# Revit family: Casement_28_E_Side_Hung_Standard
name_source: partatom
category: Windows
revit_build: Autodesk Revit 2014 (Build: 20130308_1515(x64)
units: mm (PartAtom-declared; Revit-internal decimal feet)

## types (17) — shared parameters
Aluminium Thickness = 1 mm  [stored 0.00328084 ft]
Area Pane Left Top = 0.52 m²
Bead SG Gap = 13 mm  [stored 0.0426509 ft]
Casement Dimension = 28 mm  [stored 0.0918635 ft]
Custom Sash Height = 1154 mm  [stored 3.78609 ft]
Custom Sash Width = 554 mm  [stored 1.81759 ft]
Default Sill Height = 800 mm  [stored 2.62467 ft]
Depth Bead = 14 mm  [stored 0.0459318 ft]
Description = Window 28mm, Type E side hung
Frame Center Offset = 14 mm  [stored 0.0459318 ft]
Height Panel 1 = 1139 mm  [stored 3.73688 ft]
Height Sash = 1124 mm  [stored 3.68766 ft]
Height Sash Opening = 1154 mm  [stored 3.78609 ft]
Length Transom = 540 mm  [stored 1.77165 ft]
Limit Fixed Pane Height Max = 1800 mm  [stored 5.90551 ft]
Limit Fixed Pane Height Min = 200 mm  [stored 0.656168 ft]
Limit Fixed Pane Width Max = 1500 mm  [stored 4.92126 ft]
Limit Fixed Pane Width Min = 200 mm  [stored 0.656168 ft]
Limit Sash Height Max = 1200 mm
Limit Sash Height Min = 300 mm  [stored 0.984252 ft]
Limit Sash Width Max = 600 mm  [stored 1.9685 ft]
Limit Sash Width Min = 300 mm  [stored 0.984252 ft]
Limit Window Height Max = 1860 mm
Limit Window Height Min = 1430 mm  [stored 4.6916 ft]
Limit Window Width Max = 2130 mm
Limit Window Width Min = 830 mm
Manufacturer = Crealco
Model = Casement 28
Offset Bead SG Center Reversed = 14 mm  [stored 0.0459318 ft]
Offset Mullion Left = 570 mm  [stored 1.87008 ft]
Offset Panel 3 Bead Top = 1200 mm
Offset Panel 4 Left = 600 mm  [stored 1.9685 ft]
Offset Sash Left = 23 mm  [stored 0.0754593 ft]
Offset Sash Top = 23 mm  [stored 0.0754593 ft]
Offset Transom Top = 1170 mm
Offset Window Exterior = 14 mm  [stored 0.0459318 ft]
SG Gasket Thickness = 6 mm  [stored 0.019685 ft]
Sash Center Offset = 11 mm  [stored 0.0360892 ft]
Sash Overlap = 7 mm  [stored 0.0229659 ft]
Sash Spacing Inner = 8 mm  [stored 0.0262467 ft]
Single Glazing = Yes
URL = http://www.crealco.co.za
Wall Closure = By host
Width Bead = 15 mm  [stored 0.0492126 ft]
Width Fixed Pane Bottom LHS = 540 mm  [stored 1.77165 ft]
Width Panel 1 = 540 mm  [stored 1.77165 ft]
Width Profile = 30 mm  [stored 0.0984252 ft]
Width Sash = 524 mm  [stored 1.71916 ft]
Width Sash Opening = 554 mm  [stored 1.81759 ft]
zero-valued in all types: Window Exterior Offset

## per-type parameters (varying)
| type | Area Pane Left Bottom | Area Pane Right | Clearvue SHGC Value | Clearvue U Value | Custom Windload | Custom Window Height | Custom Window Width | Depth Mullion | Energy Advantage SHGC Value | Energy Advantage U Value | Height | Height Fixed Pane Bottom LHS | Height Fixed Pane RHS | Intruderprufe LowE SHGC Value | Intruderprufe LowE U Value | Intruderprufe SHGC Value | Intruderprufe U Value | Length Mullion | Max Pane Area | Mullion Depth Windload Based | Width | Width Fixed Pane RHS | Windload Design |
| 28-0915S-1000Pa | 0.13 m² | 0.36 m² | 0.6 | 6.27 | 1000 mm  [stored 3.28084 ft] | 1490 mm  [stored 4.88845 ft] | 890 mm  [stored 2.91995 ft] | 54 mm  [stored 0.177165 ft] | 0.541 | 4.86 | 1490 mm  [stored 4.88845 ft] | 260 mm  [stored 0.853018 ft] | 1430 mm  [stored 4.6916 ft] | 0.504 | 4.77 | 0.571 | 6.2 | 1490 mm  [stored 4.88845 ft] | 0.52 m² | 54 mm  [stored 0.177165 ft] | 890 mm  [stored 2.91995 ft] | 260 mm  [stored 0.853018 ft] | 1000 mm  [stored 3.28084 ft] |
| 28-1215S-1000Pa | 0.13 m² | 0.78 m² | 0.65 | 6.18 | 1000 mm  [stored 3.28084 ft] | 1490 mm  [stored 4.88845 ft] | 1190 mm  [stored 3.9042 ft] | 54 mm  [stored 0.177165 ft] | 0.582 | 4.63 | 1490 mm  [stored 4.88845 ft] | 260 mm  [stored 0.853018 ft] | 1430 mm  [stored 4.6916 ft] | 0.545 | 4.53 | 0.617 | 6.1 | 1490 mm  [stored 4.88845 ft] | 0.78 m² | 54 mm  [stored 0.177165 ft] | 1190 mm  [stored 3.9042 ft] | 560 mm | 1000 mm  [stored 3.28084 ft] |
| 28-1215S-2000Pa | 0.13 m² | 0.78 m² | 0.723 | 6.93 | 2000 mm | 1490 mm  [stored 4.88845 ft] | 1190 mm  [stored 3.9042 ft] | 70 mm  [stored 0.229659 ft] | 0.647 | 5.23 | 1490 mm  [stored 4.88845 ft] | 260 mm  [stored 0.853018 ft] | 1430 mm  [stored 4.6916 ft] | 0.606 | 5.11 | 0.672 | 6.79 | 1490 mm  [stored 4.88845 ft] | 0.78 m² | 70 mm  [stored 0.229659 ft] | 1190 mm  [stored 3.9042 ft] | 560 mm | 2000 mm |
| 28-1515S-1000Pa | 0.13 m² | 1.21 m² | 0.68 | 6.13 | 1000 mm  [stored 3.28084 ft] | 1490 mm  [stored 4.88845 ft] | 1490 mm  [stored 4.88845 ft] | 54 mm  [stored 0.177165 ft] | 0.606 | 4.49 | 1490 mm  [stored 4.88845 ft] | 260 mm  [stored 0.853018 ft] | 1430 mm  [stored 4.6916 ft] | 0.569 | 4.38 | 0.644 | 6.04 | 1490 mm  [stored 4.88845 ft] | 1.21 m² | 54 mm  [stored 0.177165 ft] | 1490 mm  [stored 4.88845 ft] | 860 mm | 1000 mm  [stored 3.28084 ft] |
| 28-1515S-1500Pa | 0.13 m² | 1.21 m² | 0.774 | 7.03 | 1500 mm  [stored 4.92126 ft] | 1490 mm  [stored 4.88845 ft] | 1490 mm  [stored 4.88845 ft] | 70 mm  [stored 0.229659 ft] | 0.69 | 5.18 | 1490 mm  [stored 4.88845 ft] | 260 mm  [stored 0.853018 ft] | 1430 mm  [stored 4.6916 ft] | 0.647 | 5.05 | 0.721 | 6.88 | 1490 mm  [stored 4.88845 ft] | 1.21 m² | 70 mm  [stored 0.229659 ft] | 1490 mm  [stored 4.88845 ft] | 860 mm | 1500 mm  [stored 4.92126 ft] |
| 28-0918S-1000Pa | 0.29 m² | 0.43 m² | 0.616 | 6.25 | 1000 mm  [stored 3.28084 ft] | 1790 mm  [stored 5.8727 ft] | 890 mm  [stored 2.91995 ft] | 54 mm  [stored 0.177165 ft] | 0.55 | 4.8 | 1790 mm  [stored 5.8727 ft] | 560 mm | 1730 mm  [stored 5.67585 ft] | 0.518 | 4.7 | 0.584 | 6.18 | 1790 mm  [stored 5.8727 ft] | 0.52 m² | 54 mm  [stored 0.177165 ft] | 890 mm  [stored 2.91995 ft] | 260 mm  [stored 0.853018 ft] | 1000 mm  [stored 3.28084 ft] |
| 28-0918S-1500Pa | 0.29 m² | 0.43 m² | 0.692 | 7.1 | 1500 mm  [stored 4.92126 ft] | 1790 mm  [stored 5.8727 ft] | 890 mm  [stored 2.91995 ft] | 70 mm  [stored 0.229659 ft] | 0.624 | 5.49 | 1790 mm  [stored 5.8727 ft] | 560 mm | 1730 mm  [stored 5.67585 ft] | 0.581 | 5.39 | 0.639 | 6.69 | 1790 mm  [stored 5.8727 ft] | 0.52 m² | 70 mm  [stored 0.229659 ft] | 890 mm  [stored 2.91995 ft] | 260 mm  [stored 0.853018 ft] | 1500 mm  [stored 4.92126 ft] |
| 28-1218S-1000Pa | 0.29 m² | 0.95 m² | 0.666 | 6.23 | 1000 mm  [stored 3.28084 ft] | 1790 mm  [stored 5.8727 ft] | 1190 mm  [stored 3.9042 ft] | 70 mm  [stored 0.229659 ft] | 0.596 | 4.66 | 1790 mm  [stored 5.8727 ft] | 560 mm | 1730 mm  [stored 5.67585 ft] | 0.557 | 4.55 | 0.614 | 6.08 | 1790 mm  [stored 5.8727 ft] | 0.95 m² | 70 mm  [stored 0.229659 ft] | 1190 mm  [stored 3.9042 ft] | 560 mm | 1000 mm  [stored 3.28084 ft] |
| 28-1518S-1000Pa | 0.29 m² | 1.46 m² | 0 | 7.9 | 1000 mm  [stored 3.28084 ft] | 1790 mm  [stored 5.8727 ft] | 1490 mm  [stored 4.88845 ft] | 70 mm  [stored 0.229659 ft] | 0 | 7.9 | 1790 mm  [stored 5.8727 ft] | 560 mm | 1730 mm  [stored 5.67585 ft] | 0.58 | 4.4 | 0.644 | 6.02 | 1790 mm  [stored 5.8727 ft] | 1.46 m² | 70 mm  [stored 0.229659 ft] | 1490 mm  [stored 4.88845 ft] | 860 mm | 1000 mm  [stored 3.28084 ft] |
| 28-1518S-1500Pa | 0.29 m² | 1.46 m² | 0 | 7.9 | 1500 mm  [stored 4.92126 ft] | 1790 mm  [stored 5.8727 ft] | 1490 mm  [stored 4.88845 ft] | 70 mm  [stored 0.229659 ft] | 0 | 7.9 | 1790 mm  [stored 5.8727 ft] | 560 mm | 1730 mm  [stored 5.67585 ft] | 0.58 | 4.4 | 0.644 | 6.02 | 1790 mm  [stored 5.8727 ft] | 1.46 m² | 70 mm  [stored 0.229659 ft] | 1490 mm  [stored 4.88845 ft] | 860 mm | 1500 mm  [stored 4.92126 ft] |
| 28-0915S-1500Pa | 0.13 m² | 0.36 m² | 0.6 | 6.27 | 1500 mm  [stored 4.92126 ft] | 1490 mm  [stored 4.88845 ft] | 890 mm  [stored 2.91995 ft] | 54 mm  [stored 0.177165 ft] | 0.541 | 4.86 | 1490 mm  [stored 4.88845 ft] | 260 mm  [stored 0.853018 ft] | 1430 mm  [stored 4.6916 ft] | 0.504 | 4.77 | 0.571 | 6.2 | 1490 mm  [stored 4.88845 ft] | 0.52 m² | 54 mm  [stored 0.177165 ft] | 890 mm  [stored 2.91995 ft] | 260 mm  [stored 0.853018 ft] | 1500 mm  [stored 4.92126 ft] |
| 28-0915S-2000Pa | 0.13 m² | 0.36 m² | 0.6 | 6.27 | 2000 mm | 1490 mm  [stored 4.88845 ft] | 890 mm  [stored 2.91995 ft] | 54 mm  [stored 0.177165 ft] | 0.541 | 4.86 | 1490 mm  [stored 4.88845 ft] | 260 mm  [stored 0.853018 ft] | 1430 mm  [stored 4.6916 ft] | 0.504 | 4.77 | 0.571 | 6.2 | 1490 mm  [stored 4.88845 ft] | 0.52 m² | 54 mm  [stored 0.177165 ft] | 890 mm  [stored 2.91995 ft] | 260 mm  [stored 0.853018 ft] | 2000 mm |
| 28-0918S-2000Pa | 0.29 m² | 0.43 m² | 0.692 | 7.1 | 2000 mm | 1790 mm  [stored 5.8727 ft] | 890 mm  [stored 2.91995 ft] | 70 mm  [stored 0.229659 ft] | 0.624 | 5.49 | 1790 mm  [stored 5.8727 ft] | 560 mm | 1730 mm  [stored 5.67585 ft] | 0.581 | 5.39 | 0.639 | 6.69 | 1790 mm  [stored 5.8727 ft] | 0.52 m² | 70 mm  [stored 0.229659 ft] | 890 mm  [stored 2.91995 ft] | 260 mm  [stored 0.853018 ft] | 2000 mm |
| 28-1215S-1500Pa | 0.13 m² | 0.78 m² | 0.65 | 6.18 | 1500 mm  [stored 4.92126 ft] | 1490 mm  [stored 4.88845 ft] | 1190 mm  [stored 3.9042 ft] | 54 mm  [stored 0.177165 ft] | 0.582 | 4.63 | 1490 mm  [stored 4.88845 ft] | 260 mm  [stored 0.853018 ft] | 1430 mm  [stored 4.6916 ft] | 0.545 | 4.53 | 0.617 | 6.1 | 1490 mm  [stored 4.88845 ft] | 0.78 m² | 54 mm  [stored 0.177165 ft] | 1190 mm  [stored 3.9042 ft] | 560 mm | 1500 mm  [stored 4.92126 ft] |
| 28-1218S-1500Pa | 0.29 m² | 0.95 m² | 0.666 | 6.23 | 1500 mm  [stored 4.92126 ft] | 1790 mm  [stored 5.8727 ft] | 1190 mm  [stored 3.9042 ft] | 70 mm  [stored 0.229659 ft] | 0.596 | 4.66 | 1790 mm  [stored 5.8727 ft] | 560 mm | 1730 mm  [stored 5.67585 ft] | 0.557 | 4.55 | 0.614 | 6.08 | 1790 mm  [stored 5.8727 ft] | 0.95 m² | 70 mm  [stored 0.229659 ft] | 1190 mm  [stored 3.9042 ft] | 560 mm | 1500 mm  [stored 4.92126 ft] |
| 28-1218S-2000Pa | 0.29 m² | 0.95 m² | 0.666 | 6.23 | 2000 mm | 1790 mm  [stored 5.8727 ft] | 1190 mm  [stored 3.9042 ft] | 70 mm  [stored 0.229659 ft] | 0.596 | 4.66 | 1790 mm  [stored 5.8727 ft] | 560 mm | 1730 mm  [stored 5.67585 ft] | 0.557 | 4.55 | 0.614 | 6.08 | 1790 mm  [stored 5.8727 ft] | 0.95 m² | 70 mm  [stored 0.229659 ft] | 1190 mm  [stored 3.9042 ft] | 560 mm | 2000 mm |
| 28-1515S-2000Pa | 0.13 m² | 1.21 m² | 0.774 | 7.03 | 2000 mm | 1490 mm  [stored 4.88845 ft] | 1490 mm  [stored 4.88845 ft] | 70 mm  [stored 0.229659 ft] | 0.69 | 5.18 | 1490 mm  [stored 4.88845 ft] | 260 mm  [stored 0.853018 ft] | 1430 mm  [stored 4.6916 ft] | 0.647 | 5.05 | 0.721 | 6.88 | 1490 mm  [stored 4.88845 ft] | 1.21 m² | 70 mm  [stored 0.229659 ft] | 1490 mm  [stored 4.88845 ft] | 860 mm | 2000 mm |

note: [stored X ft] marks values corroborated as IEEE doubles in the binary element streams (Revit-internal decimal feet)

## geometry (parser evidence)
native form markers: Blend x4, Sweep x27
no freeform markers — native parametric forms only
